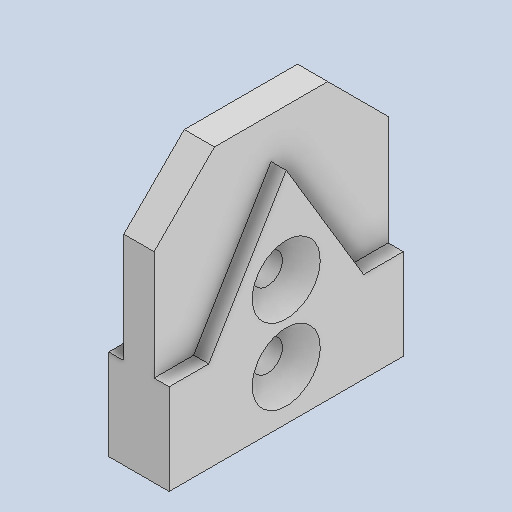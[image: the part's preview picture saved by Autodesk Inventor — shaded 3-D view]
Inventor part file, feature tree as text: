
AUTODESK INVENTOR PART (.ipt)
format: ipt  version: 2022 (Build 260153000, 153)  size: 188,928 bytes
history: native  units: in
note: dims shown in document units (in); Inventor stores cm internally (conversion verified against a paired STEP export)
features: sketch x5, extrude x4, mirror x3, other x3, hole x2, projected_geometry x2, chamfer x1
ambient origin geometry x8: Origin, YZ Plane, XZ Plane, XY Plane, X Axis, Y Axis, Z Axis, Center Point
bodies: Solid1 (feature_tree)
feature tree (20):
  extrude  "Extrusion1"  Depth=0.8858in
  extrude  "Extrusion4"  Depth=0.1575in
  mirror  "Mirror2"
  extrude  "Extrusion5"  Depth=0.0787in TaperAngle=0.0deg
  extrude  "Extrusion6"  Depth=0.3937in TaperAngle=0.0deg
  mirror  "Mirror3"
  mirror  "Mirror4"
  sketch  "Sketch9"  dims[d40=0.1575in d41=0.3937in d42=0.3937in d43=0.1575in d44=0.2362in d45=0.3543in d46=0.0787in d47=90.0deg d48=0.315in d49=0.8108in d50=0.3937in d51=0.3937in d52=0.3937in d53=0.1575in d54=0.2362in d55=0.3543in d56=0.0787in d57=90.0deg d58=0.315in d59=0.8108in d60=0.315in d61=0.0787in d62=45.0deg]
  other  "Work Point4"
  other  "Work Point5"
  hole  "Hole3"  [1 undecoded]
  other  "Work Point6"
  hole  "Hole4"  [1 undecoded]
  chamfer  "Chamfer1"  [1 undecoded]
  sketch  "Sketch1"  dims[d0=1.2205in d1=0.8858in]
  sketch  "Sketch2"  dims[d2=0.1575in d3=0.0in d31=0.8067in]
  sketch  "Sketch7"  dims[d33=0.6723in d34=0.0787in d35=0.0in]
  projected_geometry  "Projected Loop2"
  sketch  "Sketch8"  dims[d36=0.4724in d37=0.0in d38=0.3937in d39=0.0in]
  projected_geometry  "Projected Loop3"
note: 3 required parameter values undecoded (feature->parameter linkage not recoverable at this tier; creation-order binding heuristic only, values carry confidence <= 0.55)
